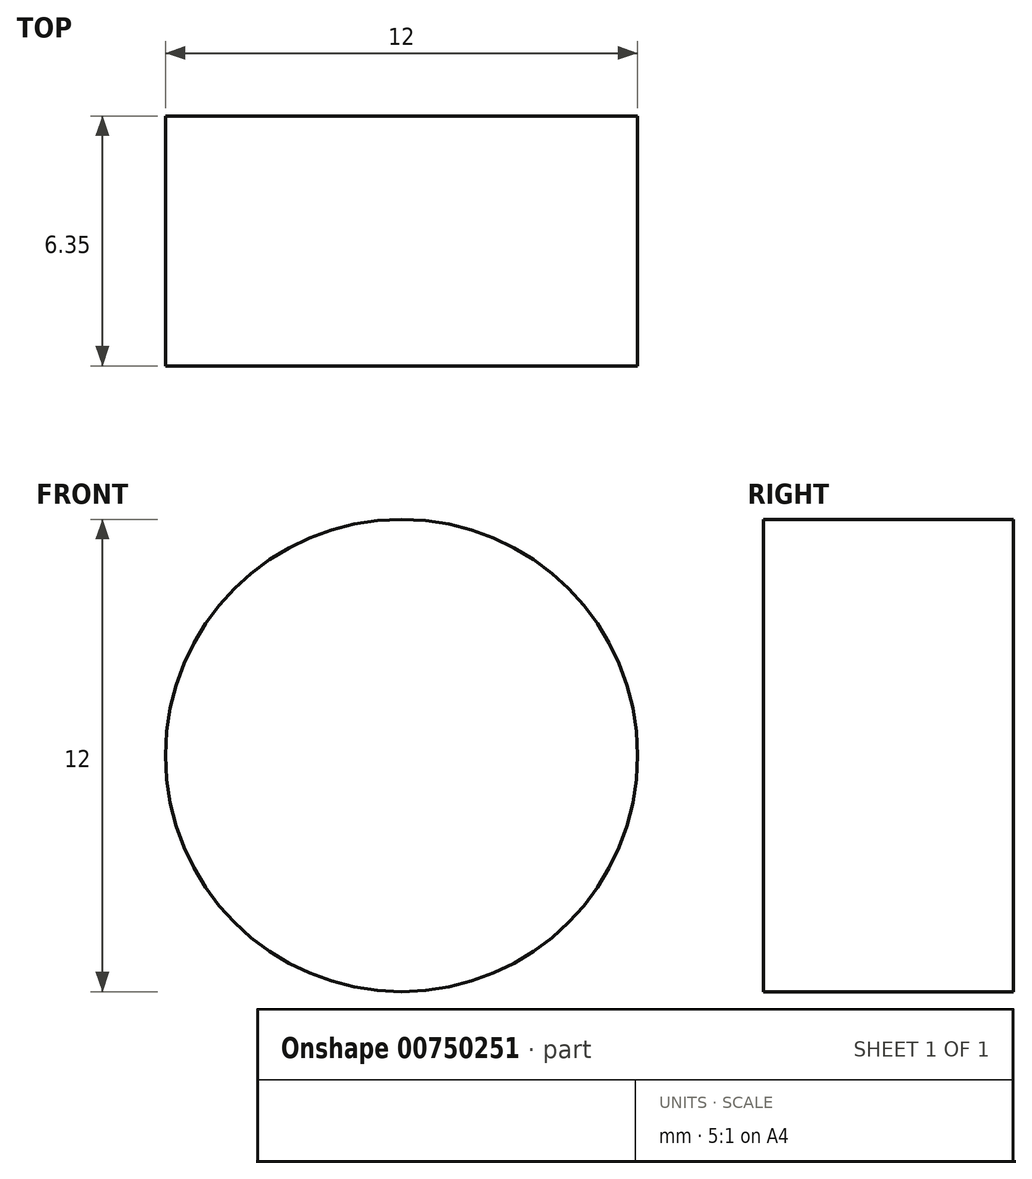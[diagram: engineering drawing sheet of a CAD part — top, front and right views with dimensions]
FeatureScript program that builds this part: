
annotation { "Feature Type Name" : "Feature", "Feature Type Description" : "" }
export const myFeature = defineFeature(function(context is Context, id is Id, definition is map)
    precondition{}
    {
        {
            var Q0;
            Q0=qCreatedBy(makeId("Front.planeOp"),FACE);
            var sketch = newSketch(context, id + "F0", { "sketchPlane" : qUnion([Q0])});
            skCircle(sketch, "E0", {"center": v(0, 0) * mm, "radius": 6 * mm});
            skSolve(sketch);
        }
        {
            var Q0;
            Q0 = qSketchRegion(id + "F0", true);
            extrude(context, id + "F1", {"entities" : qUnion([Q0]), "depth" : 6.35 * mm, "offsetDistance" : 25.4 * mm});
        }
    });
